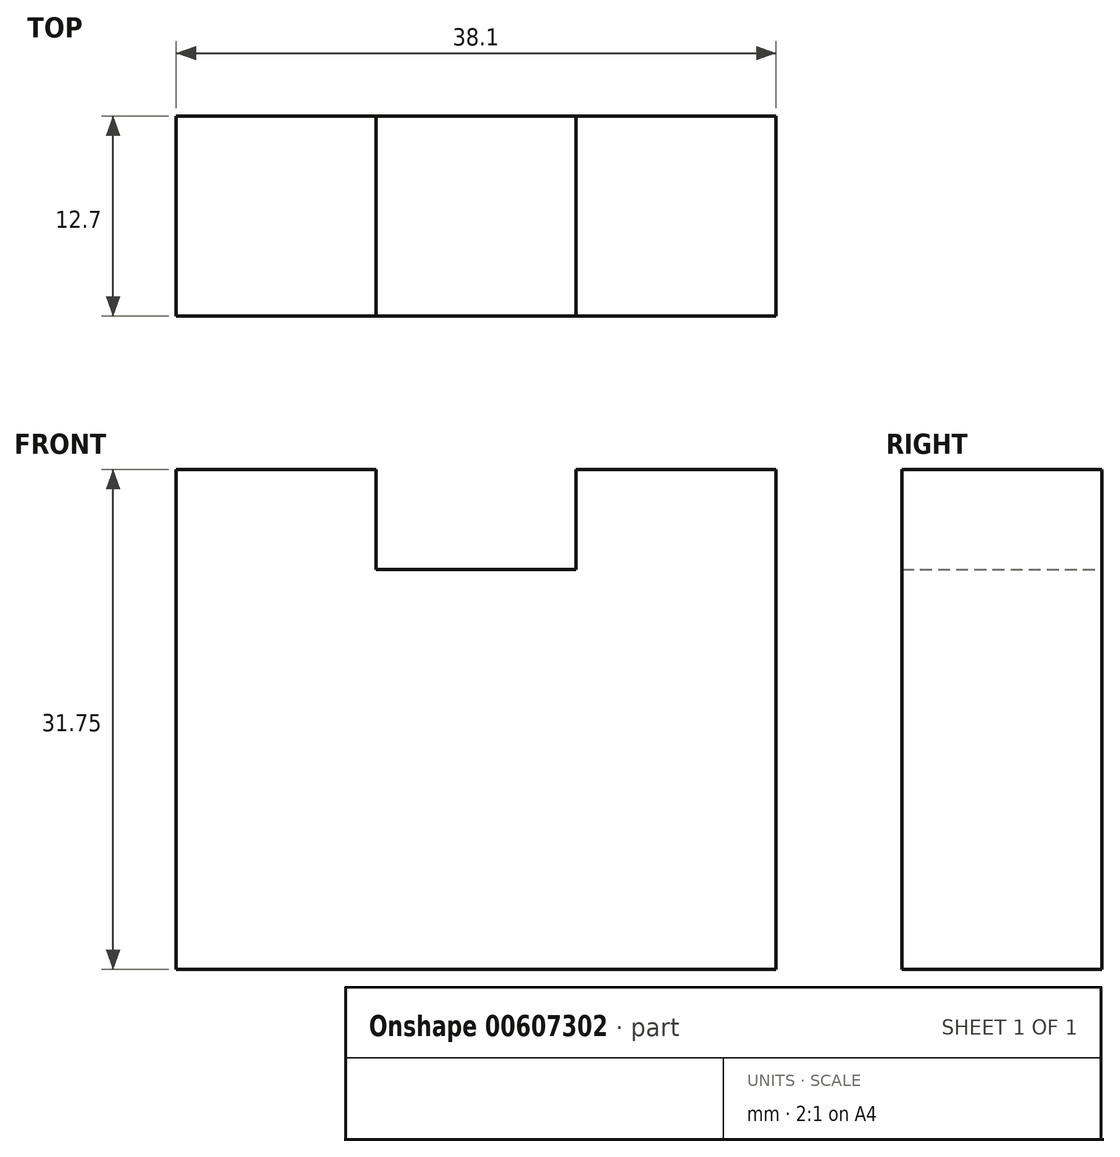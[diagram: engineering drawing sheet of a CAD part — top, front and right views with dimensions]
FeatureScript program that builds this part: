
annotation { "Feature Type Name" : "Feature", "Feature Type Description" : "" }
export const myFeature = defineFeature(function(context is Context, id is Id, definition is map)
    precondition{}
    {
        {
            var Q0;
            Q0=qCreatedBy(makeId("Front.planeOp"),FACE);
            var sketch = newSketch(context, id + "F0", { "sketchPlane" : qUnion([Q0])});
            skLineSegment(sketch, "E0", {"start": v(0, 0) * mm, "end": v(38.1, 0) * mm});
            skLineSegment(sketch, "E1", {"start": v(0, 0) * mm, "end": v(0, 31.75) * mm});
            skLineSegment(sketch, "E2", {"start": v(0, 31.75) * mm, "end": v(12.7, 31.75) * mm});
            skLineSegment(sketch, "E3", {"start": v(12.7, 31.75) * mm, "end": v(12.7, 25.4) * mm});
            skLineSegment(sketch, "E4", {"start": v(12.7, 25.4) * mm, "end": v(25.4, 25.4) * mm});
            skLineSegment(sketch, "E5", {"start": v(25.4, 25.4) * mm, "end": v(25.4, 31.75) * mm});
            skLineSegment(sketch, "E6", {"start": v(25.4, 31.75) * mm, "end": v(38.1, 31.75) * mm});
            skLineSegment(sketch, "E7", {"start": v(38.1, 31.75) * mm, "end": v(38.1, 0) * mm});
            skSolve(sketch);
        }
        {
            var Q0;
            Q0=makeQuery(id+"F0.imprint","IMPRINT",FACE,{"disambiguationData":[TD([[makeQuery(id+"F0.imprint","IMPRINT",EDGE,{"derivedFrom":sQuery(id+"F0.wireOp",EDGE,"E0")}),1.0]])]});
            extrude(context, id + "F1", {"entities" : qUnion([Q0]), "depth" : 12.7 * mm, "offsetDistance" : 25.4 * mm});
        }
    });
